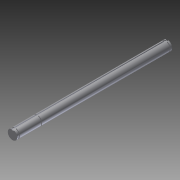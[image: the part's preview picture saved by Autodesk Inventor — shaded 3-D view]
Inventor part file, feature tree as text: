
AUTODESK INVENTOR PART (.ipt)
format: ipt  version: 2012 (Build 160160000, 160)  size: 112,640 bytes
history: native  units: in
note: dims shown in document units (in); Inventor stores cm internally (conversion verified against a paired STEP export)
features: extrude x4, sketch x4, plane x3, projected_geometry x1
ambient origin geometry x8: Origin, YZ Plane, XZ Plane, XY Plane, X Axis, Y Axis, Z Axis, Center Point
bodies: Solid1 (feature_tree)
feature tree (12):
  extrude  "Extrusion1"  Depth=6.125in TaperAngle=0.0deg
  plane  "Work Plane1"
  extrude  "Extrusion2"  Depth=0.0787in
  plane  "Work Plane2"
  extrude  "Extrusion3"  Depth=0.1481in
  plane  "Work Plane3"
  extrude  "Extrusion4"  Depth=0.03in
  sketch  "Sketch1"  dims[d0=0.375in d1=6.125in d2=0.0in]
  sketch  "Sketch2"  dims[d3=0.0787in d4=0.0787in]
  projected_geometry  "Projected Loop1"
  sketch  "Sketch3"  dims[d5=0.0394in d6=0.1481in]
  sketch  "Sketch4"  dims[d7=-0.0625in d9=0.03in d10=0.03in d11=0.0in d12=-5.145in d13=0.03in d14=0.0in d15=-0.0625in d16=0.04in d17=0.0in]
